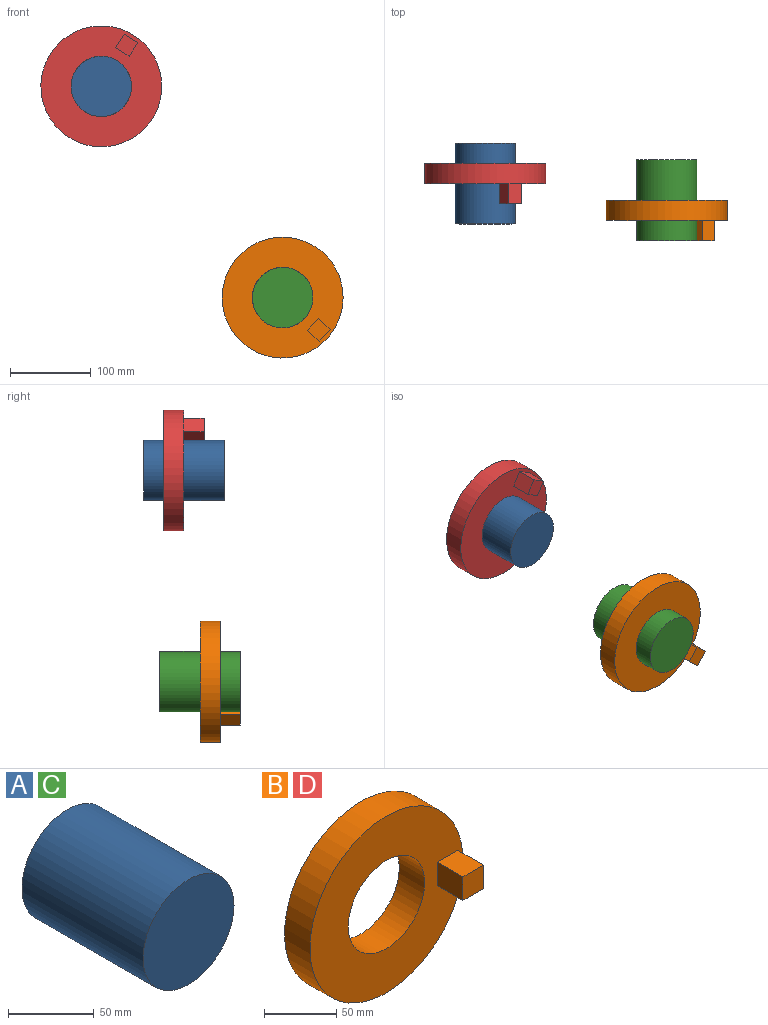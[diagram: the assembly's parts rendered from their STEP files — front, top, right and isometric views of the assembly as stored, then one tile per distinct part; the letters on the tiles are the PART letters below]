
ASSEMBLY  parts=4 mates=2
PART A: 3 faces, bbox 75x100x75 mm
  f0: cylinder r=37.5mm len=100mm, axis (0,1,0), area 23561.9mm2, adj f1,f2
  f1: plane 75x75mm, normal (0,-1,0), area 4417.9mm2, adj f0
  f2: plane 75x75mm, normal (0,1,0), area 4417.9mm2, adj f0
PART B: 9 faces, bbox 150x50x150 mm
  f0: cylinder r=75mm len=150mm, axis (0,1,0), area 11781mm2, adj f1,f2
  f1: plane 150x150mm, normal (0,-1,0), area 12853.6mm2, adj f0,f3,f4,f5,f6,f7
  f2: plane 150x150mm, normal (0,1,0), area 13253.6mm2, adj f0,f3
  f3: cylinder r=37.5mm len=75mm, axis (0,-1,0), area 5890.5mm2, adj f1,f2
  f4: plane 25x20mm, normal (1,0,0), area 500mm2, adj f1,f5,f7,f8
  f5: plane 25x20mm, normal (0,0,1), area 500mm2, adj f1,f4,f6,f8
  f6: plane 25x20mm, normal (-1,0,0), area 500mm2, adj f1,f5,f7,f8
  f7: plane 25x20mm, normal (0,0,-1), area 500mm2, adj f1,f4,f6,f8
  f8: plane 20x20mm, normal (0,-1,0), area 400mm2, adj f4,f5,f6,f7
PART C: same geometry as A
PART D: same geometry as B
PLACE A t=(-225,20.15,262.11)mm fixed
PLACE B rot(axis=(0,1,0),42.5deg) t=(0,0,0)mm
PLACE C rot(axis=(0,-1,0),15.1deg) t=(0,0,0)mm fixed
PLACE D rot(axis=(0,-1,0),57.6deg) t=(-225,45.15,262.11)mm
MATE revolute D.f0 <-> A.f0  axis (0,-1,0) through (-225,20.15,262.11)mm
MATE revolute C.f0 <-> B.f0  axis (0,1,0) through (0,0,0)mm
